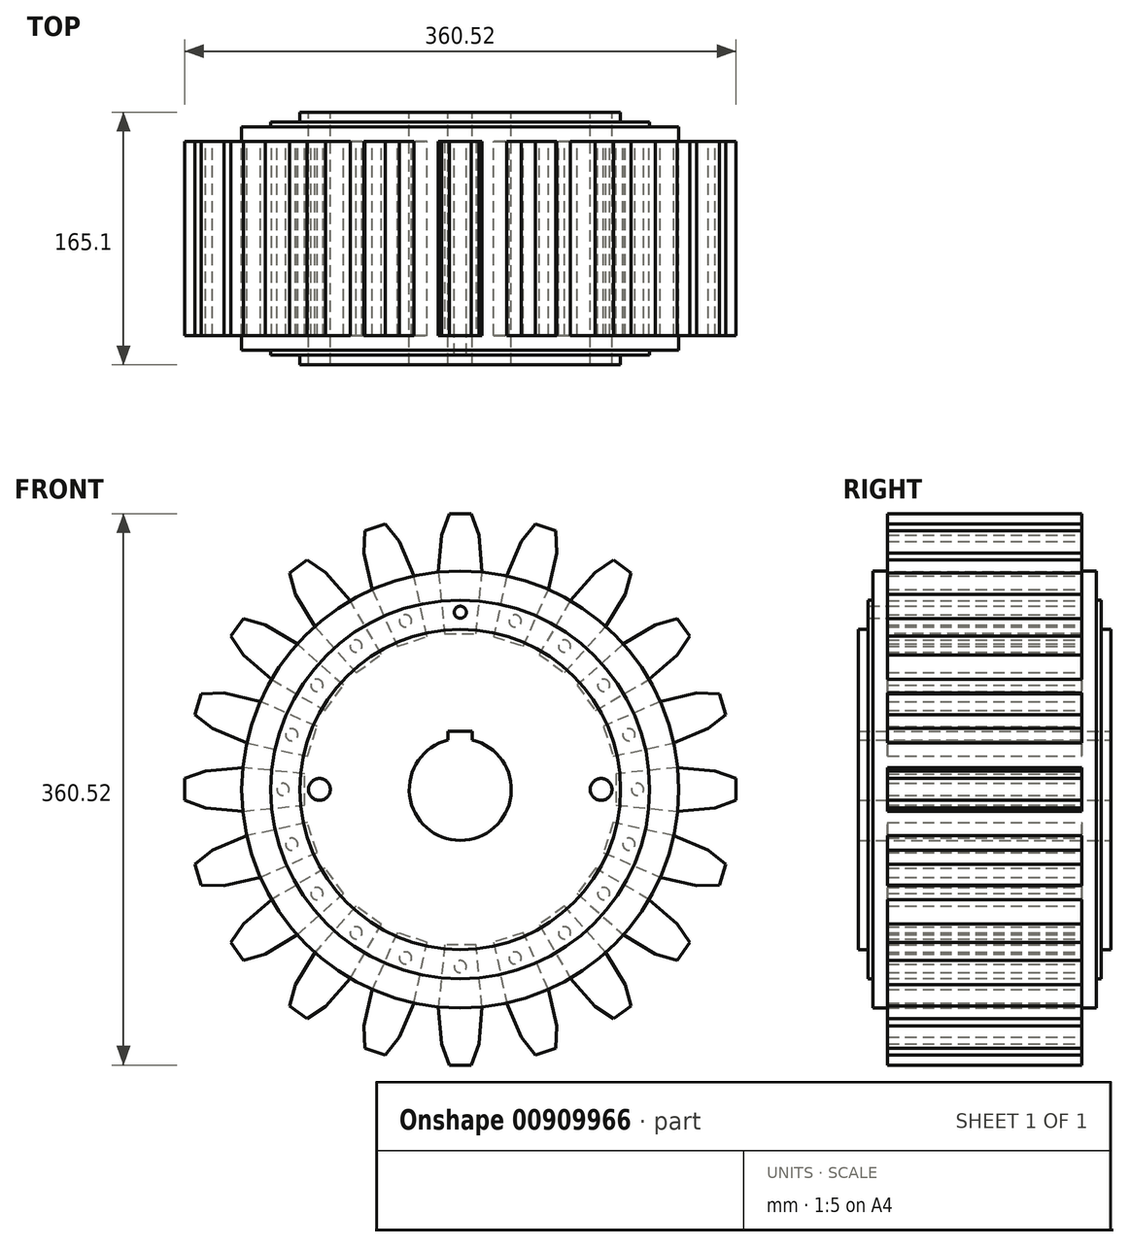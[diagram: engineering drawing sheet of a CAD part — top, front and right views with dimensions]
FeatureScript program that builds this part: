
annotation { "Feature Type Name" : "Feature", "Feature Type Description" : "" }
export const myFeature = defineFeature(function(context is Context, id is Id, definition is map)
    precondition{}
    {
        {
            var Q0;
            Q0=qCreatedBy(makeId("Front.planeOp"),FACE);
            var sketch = newSketch(context, id + "F0", { "sketchPlane" : qUnion([Q0])});
            skCircle(sketch, "E0", {"center": v(0, 0) * mm, "radius": 33.34 * mm});
            skCircle(sketch, "E1", {"center": v(0, 0) * mm, "radius": 123.83 * mm});
            skCircle(sketch, "E2", {"center": v(0, 0) * mm, "radius": 142.88 * mm});
            skLineSegment(sketch, "E3", {"start": v(-92.08, 0) * mm, "end": v(92.08, 0) * mm, "construction": true});
            skCircle(sketch, "E4", {"center": v(-92.08, 0) * mm, "radius": 7.14 * mm});
            skCircle(sketch, "E5", {"center": v(92.08, 0) * mm, "radius": 7.14 * mm});
            skLineSegment(sketch, "E6", {"start": v(-14.29, 142.16) * mm, "end": v(-10.23, 101.8) * mm});
            skLineSegment(sketch, "E7", {"start": v(-14.29, 142.16) * mm, "end": v(14.29, 142.16) * mm, "construction": true});
            skLineSegment(sketch, "E8", {"start": v(-10.23, 101.8) * mm, "end": v(10.23, 101.8) * mm});
            skLineSegment(sketch, "E9.trimOffspring", {"start": v(10.23, 101.8) * mm, "end": v(14.29, 142.16) * mm});
            skCircle(sketch, "E10", {"center": v(0, 0) * mm, "radius": 104.78 * mm});
            skLineSegment(sketch, "E11", {"start": v(14.29, 142.16) * mm, "end": v(12.16, 166.48) * mm});
            skLineSegment(sketch, "E12", {"start": v(12.16, 166.48) * mm, "end": v(7.14, 180.26) * mm});
            skLineSegment(sketch, "E13", {"start": v(7.14, 180.26) * mm, "end": v(-7.14, 180.26) * mm});
            skLineSegment(sketch, "E14", {"start": v(-7.14, 180.26) * mm, "end": v(-12.16, 166.48) * mm});
            skLineSegment(sketch, "E15", {"start": v(-12.16, 166.48) * mm, "end": v(-14.29, 142.16) * mm});
            skLineSegment(sketch, "E16", {"start": v(0, 180.26) * mm, "end": v(0, 101.8) * mm, "construction": true});
            skCircle(sketch, "E17", {"center": v(0, 115.89) * mm, "radius": 3.97 * mm});
            skLineSegment(sketch, "E18.bottom", {"start": v(-7.94, 38.1) * mm, "end": v(7.94, 38.1) * mm});
            skLineSegment(sketch, "E18.top", {"start": v(-7.94, 25.4) * mm, "end": v(7.94, 25.4) * mm});
            skLineSegment(sketch, "E18.left", {"start": v(-7.94, 38.1) * mm, "end": v(-7.94, 25.4) * mm});
            skLineSegment(sketch, "E18.right", {"start": v(7.94, 38.1) * mm, "end": v(7.94, 25.4) * mm});
            skLineSegment(sketch, "E19", {"start": v(0, 38.1) * mm, "end": v(0, 0) * mm, "construction": true});
            skSolve(sketch);
        }
        {
            var Q0;
            {var subQ5=sQuery(id+"F0.wireOp",EDGE,"E8");Q0=makeQuery(id+"F0.imprint","IMPRINT",FACE,{"disambiguationData":[TD([[makeQuery(id+"F0.imprint","IMPRINT",EDGE,{"derivedFrom":subQ5}),1.0]])]});}
            var Q1;
            {var subQ0=sQuery(id+"F0.wireOp",EDGE,"E6");var subQ1=sQuery(id+"F0.wireOp",EDGE,"E1");var subQ2=makeQuery(id+"F0.imprint","INTERSECT",VERTEX,{"derivedFrom":[subQ1,subQ0]});Q1=makeQuery(id+"F0.imprint","IMPRINT",FACE,{"disambiguationData":[TD([[makeQuery(id+"F0.imprint","IMPRINT",EDGE,{"disambiguationData":[TD([[subQ2,-1.0]])],"derivedFrom":subQ1}),1.0]])]});}
            var Q2;
            {var subQ0=sQuery(id+"F0.wireOp",EDGE,"E6");var subQ1=sQuery(id+"F0.wireOp",EDGE,"E1");var subQ2=makeQuery(id+"F0.imprint","INTERSECT",VERTEX,{"derivedFrom":[subQ1,subQ0]});Q2=makeQuery(id+"F0.imprint","IMPRINT",FACE,{"disambiguationData":[TD([[makeQuery(id+"F0.imprint","IMPRINT",EDGE,{"disambiguationData":[TD([[subQ2,1.0]])],"derivedFrom":subQ1}),1.0]])]});}
            var Q3;
            {var subQ0=sQuery(id+"F0.wireOp",EDGE,"E6");var subQ1=sQuery(id+"F0.wireOp",EDGE,"E1");var subQ2=makeQuery(id+"F0.imprint","INTERSECT",VERTEX,{"derivedFrom":[subQ1,subQ0]});Q3=makeQuery(id+"F0.imprint","IMPRINT",FACE,{"disambiguationData":[TD([[makeQuery(id+"F0.imprint","IMPRINT",EDGE,{"disambiguationData":[TD([[subQ2,-1.0]])],"derivedFrom":subQ1}),-1.0]])]});}
            var Q4;
            {var subQ0=sQuery(id+"F0.wireOp",EDGE,"E6");var subQ1=sQuery(id+"F0.wireOp",EDGE,"E1");var subQ2=makeQuery(id+"F0.imprint","INTERSECT",VERTEX,{"derivedFrom":[subQ1,subQ0]});Q4=makeQuery(id+"F0.imprint","IMPRINT",FACE,{"disambiguationData":[TD([[makeQuery(id+"F0.imprint","IMPRINT",EDGE,{"disambiguationData":[TD([[subQ2,1.0]])],"derivedFrom":subQ1}),-1.0]])]});}
            var Q5;
            Q5=makeQuery(id+"F0.imprint","IMPRINT",FACE,{"disambiguationData":[TD([[makeQuery(id+"F0.imprint","IMPRINT",EDGE,{"derivedFrom":sQuery(id+"F0.wireOp",EDGE,"E17")}),1.0]])]});
            var Q6;
            Q6=makeQuery(id+"F0.imprint","IMPRINT",FACE,{"disambiguationData":[TD([[makeQuery(id+"F0.imprint","IMPRINT",EDGE,{"derivedFrom":sQuery(id+"F0.wireOp",EDGE,"E4")}),-1.0]])]});
            extrude(context, id + "F1", {"entities" : qUnion([Q0, Q1, Q2, Q3, Q4, Q5, Q6]), "depth" : 146.05 * mm, "offsetDistance" : 25 * mm, "symmetric" : true});
        }
        {
            var Q0;
            {var subQ5=sQuery(id+"F0.wireOp",EDGE,"E8");Q0=makeQuery(id+"F0.imprint","IMPRINT",FACE,{"disambiguationData":[TD([[makeQuery(id+"F0.imprint","IMPRINT",EDGE,{"derivedFrom":subQ5}),1.0]])]});}
            var Q1;
            {var subQ0=sQuery(id+"F0.wireOp",EDGE,"E6");var subQ1=sQuery(id+"F0.wireOp",EDGE,"E1");var subQ2=makeQuery(id+"F0.imprint","INTERSECT",VERTEX,{"derivedFrom":[subQ1,subQ0]});Q1=makeQuery(id+"F0.imprint","IMPRINT",FACE,{"disambiguationData":[TD([[makeQuery(id+"F0.imprint","IMPRINT",EDGE,{"disambiguationData":[TD([[subQ2,-1.0]])],"derivedFrom":subQ1}),1.0]])]});}
            var Q2;
            {var subQ0=sQuery(id+"F0.wireOp",EDGE,"E6");var subQ1=sQuery(id+"F0.wireOp",EDGE,"E1");var subQ2=makeQuery(id+"F0.imprint","INTERSECT",VERTEX,{"derivedFrom":[subQ1,subQ0]});Q2=makeQuery(id+"F0.imprint","IMPRINT",FACE,{"disambiguationData":[TD([[makeQuery(id+"F0.imprint","IMPRINT",EDGE,{"disambiguationData":[TD([[subQ2,1.0]])],"derivedFrom":subQ1}),1.0]])]});}
            var Q3;
            Q3=makeQuery(id+"F0.imprint","IMPRINT",FACE,{"disambiguationData":[TD([[makeQuery(id+"F0.imprint","IMPRINT",EDGE,{"derivedFrom":sQuery(id+"F0.wireOp",EDGE,"E17")}),1.0]])]});
            var Q4;
            Q4=makeQuery(id+"F0.imprint","IMPRINT",FACE,{"disambiguationData":[TD([[makeQuery(id+"F0.imprint","IMPRINT",EDGE,{"derivedFrom":sQuery(id+"F0.wireOp",EDGE,"E4")}),-1.0]])]});
            extrude(context, id + "F2", {"entities" : qUnion([Q0, Q1, Q2, Q3, Q4]), "operationType" : NewBodyOperationType.ADD, "depth" : 152.4 * mm, "offsetDistance" : 25 * mm, "symmetric" : true});
        }
        {
            var Q0;
            {var subQ0=sQuery(id+"F0.wireOp",EDGE,"E8");Q0=makeQuery(id+"F0.imprint","IMPRINT",FACE,{"disambiguationData":[TD([[makeQuery(id+"F0.imprint","IMPRINT",EDGE,{"derivedFrom":subQ0}),1.0]])]});}
            var Q1;
            Q1=makeQuery(id+"F0.imprint","IMPRINT",FACE,{"disambiguationData":[TD([[makeQuery(id+"F0.imprint","IMPRINT",EDGE,{"derivedFrom":sQuery(id+"F0.wireOp",EDGE,"E4")}),-1.0]])]});
            extrude(context, id + "F3", {"entities" : qUnion([Q0, Q1]), "operationType" : NewBodyOperationType.ADD, "depth" : 165.1 * mm, "offsetDistance" : 25 * mm, "symmetric" : true});
        }
        {
            var Q0;
            {var subQ5=sQuery(id+"F0.wireOp",EDGE,"E8");Q0=makeQuery(id+"F0.imprint","IMPRINT",FACE,{"disambiguationData":[TD([[makeQuery(id+"F0.imprint","IMPRINT",EDGE,{"derivedFrom":subQ5}),1.0]])]});}
            var Q1;
            {var subQ0=sQuery(id+"F0.wireOp",EDGE,"E6");var subQ1=sQuery(id+"F0.wireOp",EDGE,"E1");var subQ2=makeQuery(id+"F0.imprint","INTERSECT",VERTEX,{"derivedFrom":[subQ1,subQ0]});Q1=makeQuery(id+"F0.imprint","IMPRINT",FACE,{"disambiguationData":[TD([[makeQuery(id+"F0.imprint","IMPRINT",EDGE,{"disambiguationData":[TD([[subQ2,1.0]])],"derivedFrom":subQ1}),-1.0]])]});}
            var Q2;
            {var subQ0=sQuery(id+"F0.wireOp",EDGE,"E6");var subQ1=sQuery(id+"F0.wireOp",EDGE,"E1");var subQ2=makeQuery(id+"F0.imprint","INTERSECT",VERTEX,{"derivedFrom":[subQ1,subQ0]});Q2=makeQuery(id+"F0.imprint","IMPRINT",FACE,{"disambiguationData":[TD([[makeQuery(id+"F0.imprint","IMPRINT",EDGE,{"disambiguationData":[TD([[subQ2,1.0]])],"derivedFrom":subQ1}),1.0]])]});}
            var Q3;
            Q3=makeQuery(id+"F0.imprint","IMPRINT",FACE,{"disambiguationData":[TD([[makeQuery(id+"F0.imprint","IMPRINT",EDGE,{"derivedFrom":sQuery(id+"F0.wireOp",EDGE,"E17")}),1.0]])]});
            extrude(context, id + "F4", {"entities" : qUnion([Q0, Q1, Q2, Q3]), "operationType" : NewBodyOperationType.REMOVE, "oppositeDirection" : true, "depth" : 127 * mm, "offsetDistance" : 25 * mm, "symmetric" : true});
        }
        {
            var Q0;
            Q0=makeQuery(id+"F0.imprint","IMPRINT",FACE,{"disambiguationData":[TD([[makeQuery(id+"F0.imprint","IMPRINT",EDGE,{"derivedFrom":sQuery(id+"F0.wireOp",EDGE,"E17")}),1.0]])]});
            extrude(context, id + "F5", {"entities" : qUnion([Q0]), "operationType" : NewBodyOperationType.REMOVE, "endBound" : BoundingType.THROUGH_ALL, "depth" : 25 * mm, "offsetDistance" : 25 * mm});
        }
        {
            var Q0;
            {var subQ0=sQuery(id+"F0.wireOp",EDGE,"E6");var subQ1=sQuery(id+"F0.wireOp",EDGE,"E1");var subQ2=makeQuery(id+"F0.imprint","INTERSECT",VERTEX,{"derivedFrom":[subQ1,subQ0]});Q0=makeQuery(id+"F0.imprint","IMPRINT",FACE,{"disambiguationData":[TD([[makeQuery(id+"F0.imprint","IMPRINT",EDGE,{"disambiguationData":[TD([[subQ2,1.0]])],"derivedFrom":subQ1}),-1.0]])]});}
            var Q1;
            {var subQ0=sQuery(id+"F0.wireOp",EDGE,"E6");var subQ1=sQuery(id+"F0.wireOp",EDGE,"E1");var subQ2=makeQuery(id+"F0.imprint","INTERSECT",VERTEX,{"derivedFrom":[subQ1,subQ0]});Q1=makeQuery(id+"F0.imprint","IMPRINT",FACE,{"disambiguationData":[TD([[makeQuery(id+"F0.imprint","IMPRINT",EDGE,{"disambiguationData":[TD([[subQ2,1.0]])],"derivedFrom":subQ1}),1.0]])]});}
            var Q2;
            {var subQ0=sQuery(id+"F0.wireOp",EDGE,"E8");Q2=makeQuery(id+"F0.imprint","IMPRINT",FACE,{"disambiguationData":[TD([[makeQuery(id+"F0.imprint","IMPRINT",EDGE,{"derivedFrom":subQ0}),1.0]])]});}
            var Q3;
            {var subQ0=sQuery(id+"F0.wireOp",EDGE,"E11");Q3=makeQuery(id+"F0.imprint","IMPRINT",FACE,{"disambiguationData":[TD([[makeQuery(id+"F0.imprint","IMPRINT",EDGE,{"derivedFrom":subQ0}),1.0]])]});}
            extrude(context, id + "F6", {"entities" : qUnion([Q0, Q1, Q2, Q3]), "depth" : 127 * mm, "offsetDistance" : 25 * mm, "symmetric" : true});
        }
        {
            var Q0;
            Q0=makeQuery(id+"F6.opExtrude","SWEPT_BODY",BODY,{"disambiguationData":[OSD([sQuery(id+"F0.wireOp",EDGE,"E6"),sQuery(id+"F0.wireOp",EDGE,"E8"),sQuery(id+"F0.wireOp",EDGE,"E9.trimOffspring"),sQuery(id+"F0.wireOp",EDGE,"E11"),sQuery(id+"F0.wireOp",EDGE,"E12"),sQuery(id+"F0.wireOp",EDGE,"E13"),sQuery(id+"F0.wireOp",EDGE,"E14"),sQuery(id+"F0.wireOp",EDGE,"E15")])]});
            var Q1;
            Q1=makeQuery(id+"F3.opExtrude","CAP_EDGE",EDGE,{"disambiguationData":[OSD([sQuery(id+"F0.wireOp",EDGE,"E0")])],"isStart":true});
            circularPattern(context, id + "F7", {"entities" : qUnion([Q0]), "axis" : qUnion([Q1]), "angle" : 360 * degree, "instanceCount" : 20, "equalSpace" : true});
        }
    });
